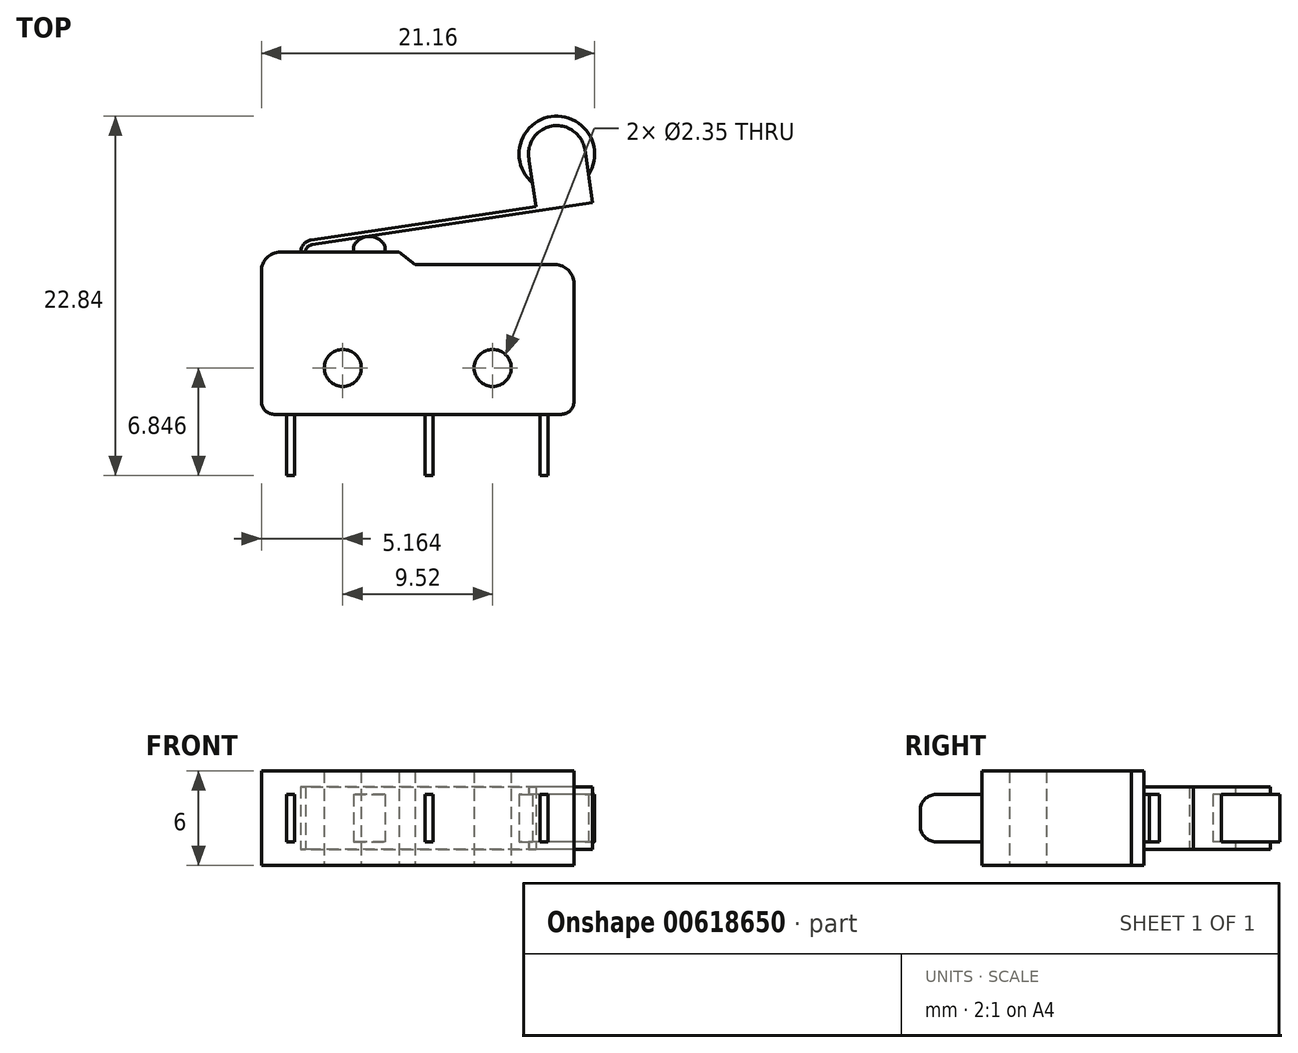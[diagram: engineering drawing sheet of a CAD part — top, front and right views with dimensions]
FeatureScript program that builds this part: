
annotation { "Feature Type Name" : "Feature", "Feature Type Description" : "" }
export const myFeature = defineFeature(function(context is Context, id is Id, definition is map)
    precondition{}
    {
        {
            var Q0;
            Q0=qCreatedBy(makeId("Top.planeOp"),FACE);
            var sketch = newSketch(context, id + "F0", { "sketchPlane" : qUnion([Q0])});
            skLineSegment(sketch, "E0", {"start": v(-0.83, 1.98) * mm, "end": v(8.07, 1.98) * mm});
            skLineSegment(sketch, "E1", {"start": v(9.27, 0.78) * mm, "end": v(9.27, -6.72) * mm});
            skLineSegment(sketch, "E2", {"start": v(8.47, -7.52) * mm, "end": v(-9.78, -7.52) * mm});
            skLineSegment(sketch, "E3", {"start": v(-10.58, -6.72) * mm, "end": v(-10.58, 1.58) * mm});
            skLineSegment(sketch, "E4", {"start": v(-9.38, 2.78) * mm, "end": v(-1.83, 2.78) * mm});
            skLineSegment(sketch, "E5", {"start": v(-1.83, 2.78) * mm, "end": v(-0.83, 1.98) * mm});
            skLineSegment(sketch, "E6.bottom", {"start": v(7.12, -11.42) * mm, "end": v(7.62, -11.42) * mm});
            skLineSegment(sketch, "E6.top", {"start": v(7.12, -7.52) * mm, "end": v(7.62, -7.52) * mm});
            skLineSegment(sketch, "E6.left", {"start": v(7.12, -11.42) * mm, "end": v(7.12, -7.52) * mm});
            skLineSegment(sketch, "E6.right", {"start": v(7.62, -11.42) * mm, "end": v(7.62, -7.52) * mm});
            skLineSegment(sketch, "E7.bottom", {"start": v(-0.18, -11.42) * mm, "end": v(0.32, -11.42) * mm});
            skLineSegment(sketch, "E7.top", {"start": v(-0.18, -7.52) * mm, "end": v(0.32, -7.52) * mm});
            skLineSegment(sketch, "E7.left", {"start": v(-0.18, -11.42) * mm, "end": v(-0.18, -7.52) * mm});
            skLineSegment(sketch, "E7.right", {"start": v(0.32, -11.42) * mm, "end": v(0.32, -7.52) * mm});
            skLineSegment(sketch, "E8.bottom", {"start": v(-8.98, -11.42) * mm, "end": v(-8.48, -11.42) * mm});
            skLineSegment(sketch, "E8.top", {"start": v(-8.98, -7.52) * mm, "end": v(-8.48, -7.52) * mm});
            skLineSegment(sketch, "E8.left", {"start": v(-8.98, -11.42) * mm, "end": v(-8.98, -7.52) * mm});
            skLineSegment(sketch, "E8.right", {"start": v(-8.48, -11.42) * mm, "end": v(-8.48, -7.52) * mm});
            skLineSegment(sketch, "E9", {"start": v(10.46, 5.92) * mm, "end": v(-7.38, 3.25) * mm});
            skLineSegment(sketch, "E10", {"start": v(-7.42, 3.55) * mm, "end": v(6.86, 5.69) * mm});
            skLineSegment(sketch, "E11", {"start": v(6.86, 5.69) * mm, "end": v(6.42, 8.6) * mm});
            skLineSegment(sketch, "E12", {"start": v(10.46, 5.92) * mm, "end": v(9.96, 9.29) * mm});
            skArc(sketch, "E13", {"start": v(9.96, 9.29) * mm, "mid": v(7.84, 10.79) * mm, "end": v(6.42, 8.6) * mm});
            skCircle(sketch, "E14", {"center": v(8.18, 9.02) * mm, "radius": 2.4 * mm});
            skPoint(sketch, "E15.visualSharp", {"position": v(-10.58, 2.78) * mm});
            skArc(sketch, "E15.filletArc", {"start": v(-9.38, 2.78) * mm, "mid": v(-10.23, 2.43) * mm, "end": v(-10.58, 1.58) * mm});
            skPoint(sketch, "E16.visualSharp", {"position": v(-10.58, -7.52) * mm});
            skArc(sketch, "E16.filletArc", {"start": v(-10.58, -6.72) * mm, "mid": v(-10.35, -7.28) * mm, "end": v(-9.78, -7.52) * mm});
            skPoint(sketch, "E17.visualSharp", {"position": v(9.27, -7.52) * mm});
            skArc(sketch, "E17.filletArc", {"start": v(8.47, -7.52) * mm, "mid": v(9.03, -7.28) * mm, "end": v(9.27, -6.72) * mm});
            skPoint(sketch, "E18.visualSharp", {"position": v(9.27, 1.98) * mm});
            skArc(sketch, "E18.filletArc", {"start": v(9.27, 0.78) * mm, "mid": v(8.92, 1.63) * mm, "end": v(8.07, 1.98) * mm});
            skArc(sketch, "E19", {"start": v(-7.38, 3.25) * mm, "mid": v(-7.67, 3.1) * mm, "end": v(-7.78, 2.78) * mm});
            skArc(sketch, "E20", {"start": v(-7.42, 3.55) * mm, "mid": v(-7.9, 3.29) * mm, "end": v(-8.08, 2.78) * mm});
            skCircle(sketch, "E21", {"center": v(8.18, 9.02) * mm, "radius": 1.49 * mm});
            skLineSegment(sketch, "E22", {"start": v(-4.73, 2.78) * mm, "end": v(-4.73, 3.14) * mm});
            skLineSegment(sketch, "E23", {"start": v(-2.73, 2.78) * mm, "end": v(-2.73, 3.14) * mm});
            skArc(sketch, "E24", {"start": v(-2.73, 3.14) * mm, "mid": v(-3.73, 3.78) * mm, "end": v(-4.73, 3.14) * mm});
            skCircle(sketch, "E25", {"center": v(4.1, -4.57) * mm, "radius": 1.18 * mm});
            skCircle(sketch, "E26", {"center": v(-5.42, -4.57) * mm, "radius": 1.18 * mm});
            skSolve(sketch);
        }
        {
            var Q0;
            {var subQ0=sQuery(id+"F0.wireOp",EDGE,"E13");Q0=makeQuery(id+"F0.imprint","IMPRINT",FACE,{"disambiguationData":[TD([[makeQuery(id+"F0.imprint","IMPRINT",EDGE,{"derivedFrom":subQ0}),-1.0]])]});}
            var Q1;
            {var subQ5=sQuery(id+"F0.wireOp",EDGE,"E13");Q1=makeQuery(id+"F0.imprint","IMPRINT",FACE,{"disambiguationData":[TD([[makeQuery(id+"F0.imprint","IMPRINT",EDGE,{"derivedFrom":subQ5}),1.0]])]});}
            extrude(context, id + "F1", {"entities" : qUnion([Q0, Q1]), "endBound" : BoundingType.SYMMETRIC, "depth" : 3 * mm, "offsetDistance" : 25 * mm});
        }
        {
            var Q0;
            {var subQ5=sQuery(id+"F0.wireOp",EDGE,"E9");Q0=makeQuery(id+"F0.imprint","IMPRINT",FACE,{"disambiguationData":[TD([[makeQuery(id+"F0.imprint","IMPRINT",EDGE,{"derivedFrom":subQ5}),-1.0]])]});}
            var Q1;
            {var subQ5=sQuery(id+"F0.wireOp",EDGE,"E13");Q1=makeQuery(id+"F0.imprint","IMPRINT",FACE,{"disambiguationData":[TD([[makeQuery(id+"F0.imprint","IMPRINT",EDGE,{"derivedFrom":subQ5}),1.0]])]});}
            var Q2;
            Q2=makeQuery(id+"F0.imprint","IMPRINT",FACE,{"disambiguationData":[TD([[makeQuery(id+"F0.imprint","IMPRINT",EDGE,{"derivedFrom":sQuery(id+"F0.wireOp",EDGE,"E21")}),1.0]])]});
            extrude(context, id + "F2", {"entities" : qUnion([Q0, Q1, Q2]), "operationType" : NewBodyOperationType.ADD, "endBound" : BoundingType.SYMMETRIC, "depth" : 4 * mm, "offsetDistance" : 25 * mm});
        }
        {
            var Q0;
            Q0=makeQuery(id+"F0.imprint","IMPRINT",FACE,{"disambiguationData":[TD([[makeQuery(id+"F0.imprint","IMPRINT",EDGE,{"derivedFrom":sQuery(id+"F0.wireOp",EDGE,"E0")}),-1.0]])]});
            extrude(context, id + "F3", {"entities" : qUnion([Q0]), "operationType" : NewBodyOperationType.ADD, "endBound" : BoundingType.SYMMETRIC, "depth" : 6 * mm, "offsetDistance" : 25 * mm});
        }
        {
            var Q0;
            Q0=makeQuery(id+"F0.imprint","IMPRINT",FACE,{"disambiguationData":[TD([[makeQuery(id+"F0.imprint","IMPRINT",EDGE,{"derivedFrom":sQuery(id+"F0.wireOp",EDGE,"E6.bottom")}),1.0]])]});
            var Q1;
            Q1=makeQuery(id+"F0.imprint","IMPRINT",FACE,{"disambiguationData":[TD([[makeQuery(id+"F0.imprint","IMPRINT",EDGE,{"derivedFrom":sQuery(id+"F0.wireOp",EDGE,"E7.bottom")}),1.0]])]});
            var Q2;
            Q2=makeQuery(id+"F0.imprint","IMPRINT",FACE,{"disambiguationData":[TD([[makeQuery(id+"F0.imprint","IMPRINT",EDGE,{"derivedFrom":sQuery(id+"F0.wireOp",EDGE,"E8.bottom")}),1.0]])]});
            var Q3;
            {var subQ0=sQuery(id+"F0.wireOp",EDGE,"E22");Q3=makeQuery(id+"F0.imprint","IMPRINT",FACE,{"disambiguationData":[TD([[makeQuery(id+"F0.imprint","IMPRINT",EDGE,{"derivedFrom":subQ0}),-1.0]])]});}
            extrude(context, id + "F4", {"entities" : qUnion([Q0, Q1, Q2, Q3]), "operationType" : NewBodyOperationType.ADD, "endBound" : BoundingType.SYMMETRIC, "depth" : 3 * mm, "offsetDistance" : 25 * mm});
        }
        {
            var Q0;
            Q0=makeQuery(id+"F4.opExtrude","CAP_EDGE",EDGE,{"disambiguationData":[OSD([sQuery(id+"F0.wireOp",EDGE,"E8.bottom")])],"isStart":false});
            var Q1;
            Q1=makeQuery(id+"F4.opExtrude","CAP_EDGE",EDGE,{"disambiguationData":[OSD([sQuery(id+"F0.wireOp",EDGE,"E7.bottom")])],"isStart":false});
            var Q2;
            Q2=makeQuery(id+"F4.opExtrude","CAP_EDGE",EDGE,{"disambiguationData":[OSD([sQuery(id+"F0.wireOp",EDGE,"E6.bottom")])],"isStart":false});
            var Q3;
            Q3=makeQuery(id+"F4.opExtrude","CAP_EDGE",EDGE,{"disambiguationData":[OSD([sQuery(id+"F0.wireOp",EDGE,"E6.bottom")])],"isStart":true});
            var Q4;
            Q4=makeQuery(id+"F4.opExtrude","CAP_EDGE",EDGE,{"disambiguationData":[OSD([sQuery(id+"F0.wireOp",EDGE,"E7.bottom")])],"isStart":true});
            var Q5;
            Q5=makeQuery(id+"F4.opExtrude","CAP_EDGE",EDGE,{"disambiguationData":[OSD([sQuery(id+"F0.wireOp",EDGE,"E8.bottom")])],"isStart":true});
            fillet(context, id + "F5", {"entities" : qUnion([Q0, Q1, Q2, Q3, Q4, Q5]), "radius" : 1 * mm, "tangentPropagation" : true, "allowEdgeOverflow" : false});
        }
    });
